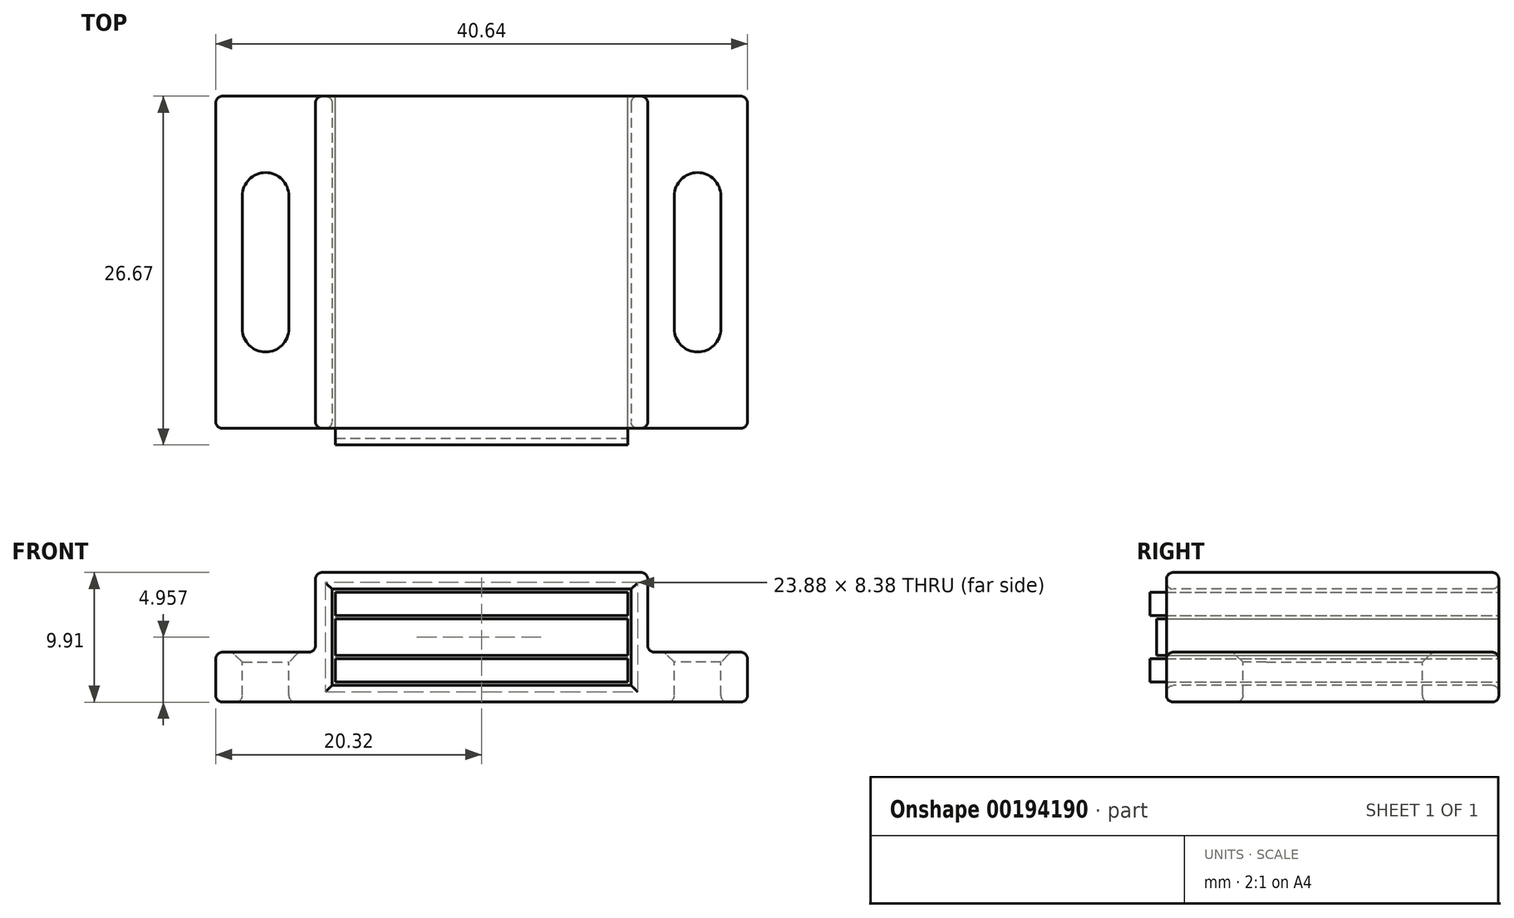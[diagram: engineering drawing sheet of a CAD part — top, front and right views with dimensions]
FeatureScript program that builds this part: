
annotation { "Feature Type Name" : "Feature", "Feature Type Description" : "" }
export const myFeature = defineFeature(function(context is Context, id is Id, definition is map)
    precondition{}
    {
        {
            var Q0;
            Q0=qCreatedBy(makeId("Front.planeOp"),FACE);
            var sketch = newSketch(context, id + "F0", { "sketchPlane" : qUnion([Q0])});
            skLineSegment(sketch, "E0", {"start": v(0, -9.9) * mm, "end": v(-40.64, -9.9) * mm});
            skLineSegment(sketch, "E1", {"start": v(-20.32, -9.9) * mm, "end": v(-20.32, 0) * mm, "construction": true});
            skLineSegment(sketch, "E2", {"start": v(-40.64, -9.9) * mm, "end": v(-40.64, -6.1) * mm});
            skLineSegment(sketch, "E3", {"start": v(-40.64, -6.1) * mm, "end": v(-33.02, -6.1) * mm});
            skLineSegment(sketch, "E4", {"start": v(-33.02, -6.1) * mm, "end": v(-33.02, 0) * mm});
            skLineSegment(sketch, "E5.MirrorCS", {"start": v(0, -9.9) * mm, "end": v(0, -6.1) * mm});
            skLineSegment(sketch, "E6.MirrorCS", {"start": v(0, -6.1) * mm, "end": v(-7.62, -6.1) * mm});
            skLineSegment(sketch, "E7.MirrorCS", {"start": v(-7.62, -6.1) * mm, "end": v(-7.62, 0) * mm});
            skLineSegment(sketch, "E8", {"start": v(-33.02, 0) * mm, "end": v(-7.62, 0) * mm});
            skLineSegment(sketch, "E9.0", {"start": v(-8.9, -8.64) * mm, "end": v(-8.9, -1.27) * mm});
            skLineSegment(sketch, "E9.1", {"start": v(-31.75, -1.27) * mm, "end": v(-8.89, -1.27) * mm});
            skLineSegment(sketch, "E9.2", {"start": v(-31.75, -8.64) * mm, "end": v(-31.75, -1.27) * mm});
            skLineSegment(sketch, "E10.0", {"start": v(-8.9, -8.64) * mm, "end": v(-31.75, -8.64) * mm});
            skSolve(sketch);
        }
        {
            var Q0;
            Q0=makeQuery(id+"F0.imprint","IMPRINT",FACE,{"disambiguationData":[TD([[makeQuery(id+"F0.imprint","IMPRINT",EDGE,{"derivedFrom":sQuery(id+"F0.wireOp",EDGE,"E0")}),-1.0]])]});
            extrude(context, id + "F1", {"entities" : qUnion([Q0]), "oppositeDirection" : true, "depth" : 25.4 * mm});
        }
        {
            var Q0;
            Q0=makeQuery(id+"F1.opExtrude","SWEPT_FACE",FACE,{"disambiguationData":[OSD([sQuery(id+"F0.wireOp",EDGE,"E8")])]});
            var sketch = newSketch(context, id + "F2", { "sketchPlane" : qUnion([Q0])});
            skLineSegment(sketch, "E11.0", {"start": v(-40.64, 25.4) * mm, "end": v(-40.64, 0) * mm, "construction": true});
            skLineSegment(sketch, "E11.1", {"start": v(-33.02, 25.4) * mm, "end": v(-33.02, 0) * mm, "construction": true});
            skLineSegment(sketch, "E11.2", {"start": v(-7.62, 25.4) * mm, "end": v(-7.62, 0) * mm, "construction": true});
            skLineSegment(sketch, "E11.3", {"start": v(0, 25.4) * mm, "end": v(0, 0) * mm, "construction": true});
            skLineSegment(sketch, "E12.0", {"start": v(-38.6, 17.78) * mm, "end": v(-38.6, 7.62) * mm});
            skLineSegment(sketch, "E13.0", {"start": v(-35.05, 17.78) * mm, "end": v(-35.05, 7.62) * mm});
            skLineSegment(sketch, "E14", {"start": v(-33.02, 25.4) * mm, "end": v(-7.62, 25.4) * mm, "construction": true});
            skLineSegment(sketch, "E15", {"start": v(-20.32, 25.4) * mm, "end": v(-20.32, 0) * mm, "construction": true});
            skArc(sketch, "E16", {"start": v(-35.05, 17.78) * mm, "mid": v(-36.83, 19.56) * mm, "end": v(-38.6, 17.78) * mm});
            skArc(sketch, "E17", {"start": v(-38.6, 7.62) * mm, "mid": v(-36.83, 5.84) * mm, "end": v(-35.05, 7.62) * mm});
            skLineSegment(sketch, "E18.MirrorCS", {"start": v(-2.03, 17.78) * mm, "end": v(-2.03, 7.62) * mm});
            skLineSegment(sketch, "E19.MirrorCS", {"start": v(-5.59, 17.78) * mm, "end": v(-5.59, 7.62) * mm});
            skArc(sketch, "E20.MirrorCS", {"start": v(-5.59, 17.78) * mm, "mid": v(-3.81, 19.56) * mm, "end": v(-2.03, 17.78) * mm});
            skArc(sketch, "E21.MirrorCS", {"start": v(-2.03, 7.62) * mm, "mid": v(-3.81, 5.84) * mm, "end": v(-5.59, 7.62) * mm});
            skSolve(sketch);
        }
        {
            var Q0;
            Q0=makeQuery(id+"F2.imprint","IMPRINT",FACE,{"disambiguationData":[TD([[makeQuery(id+"F2.imprint","IMPRINT",EDGE,{"derivedFrom":sQuery(id+"F2.wireOp",EDGE,"E12.0")}),1.0]])]});
            var Q1;
            Q1=makeQuery(id+"F2.imprint","IMPRINT",FACE,{"disambiguationData":[TD([[makeQuery(id+"F2.imprint","IMPRINT",EDGE,{"derivedFrom":sQuery(id+"F2.wireOp",EDGE,"E18.MirrorCS")}),-1.0]])]});
            extrude(context, id + "F3", {"entities" : qUnion([Q0, Q1]), "operationType" : NewBodyOperationType.REMOVE, "endBound" : BoundingType.THROUGH_ALL, "oppositeDirection" : true, "depth" : 25.4 * mm});
        }
        {
            var Q0;
            Q0=makeQuery(id+"F1.opExtrude","CAP_FACE",FACE,{"disambiguationData":[OSD([sQuery(id+"F0.wireOp",EDGE,"E0"),sQuery(id+"F0.wireOp",EDGE,"E2"),sQuery(id+"F0.wireOp",EDGE,"E3"),sQuery(id+"F0.wireOp",EDGE,"E4"),sQuery(id+"F0.wireOp",EDGE,"E5.MirrorCS"),sQuery(id+"F0.wireOp",EDGE,"E6.MirrorCS"),sQuery(id+"F0.wireOp",EDGE,"E7.MirrorCS"),sQuery(id+"F0.wireOp",EDGE,"E8"),sQuery(id+"F0.wireOp",EDGE,"E9.0"),sQuery(id+"F0.wireOp",EDGE,"E9.1"),sQuery(id+"F0.wireOp",EDGE,"E9.2"),sQuery(id+"F0.wireOp",EDGE,"E10.0")])],"isStart":true});
            var sketch = newSketch(context, id + "F4", { "sketchPlane" : qUnion([Q0])});
            skLineSegment(sketch, "E22.0", {"start": v(-31.75, -8.64) * mm, "end": v(-31.75, -1.27) * mm, "construction": true});
            skLineSegment(sketch, "E22.1", {"start": v(-31.75, -1.27) * mm, "end": v(-8.89, -1.27) * mm, "construction": true});
            skLineSegment(sketch, "E22.2", {"start": v(-8.9, -8.64) * mm, "end": v(-8.9, -1.27) * mm, "construction": true});
            skLineSegment(sketch, "E22.3", {"start": v(-8.9, -8.64) * mm, "end": v(-31.75, -8.64) * mm, "construction": true});
            skLineSegment(sketch, "E23.0", {"start": v(-9.14, -3.3) * mm, "end": v(-9.14, -1.52) * mm});
            skLineSegment(sketch, "E23.1", {"start": v(-31.5, -1.52) * mm, "end": v(-9.14, -1.52) * mm});
            skLineSegment(sketch, "E23.2", {"start": v(-31.5, -3.3) * mm, "end": v(-31.5, -1.52) * mm});
            skLineSegment(sketch, "E24", {"start": v(-31.5, -3.3) * mm, "end": v(-9.14, -3.3) * mm});
            skLineSegment(sketch, "E25", {"start": v(-31.75, -4.95) * mm, "end": v(-8.9, -4.95) * mm, "construction": true});
            skLineSegment(sketch, "E26.MirrorCS", {"start": v(-31.5, -8.38) * mm, "end": v(-9.14, -8.38) * mm});
            skLineSegment(sketch, "E27.MirrorCS", {"start": v(-31.5, -6.6) * mm, "end": v(-31.5, -8.38) * mm});
            skLineSegment(sketch, "E28.MirrorCS", {"start": v(-31.5, -6.6) * mm, "end": v(-9.14, -6.6) * mm});
            skLineSegment(sketch, "E29.MirrorCS", {"start": v(-9.14, -6.6) * mm, "end": v(-9.14, -8.38) * mm});
            skLineSegment(sketch, "E30.0", {"start": v(-31.5, -3.56) * mm, "end": v(-9.14, -3.56) * mm});
            skLineSegment(sketch, "E31.MirrorCS", {"start": v(-31.75, -2.16) * mm, "end": v(-8.9, -2.16) * mm, "construction": true});
            skLineSegment(sketch, "E32.MirrorCS", {"start": v(-31.5, -6.35) * mm, "end": v(-9.14, -6.35) * mm});
            skLineSegment(sketch, "E33", {"start": v(-31.5, -3.56) * mm, "end": v(-31.5, -6.35) * mm});
            skLineSegment(sketch, "E34", {"start": v(-9.14, -3.56) * mm, "end": v(-9.14, -6.35) * mm});
            skSolve(sketch);
        }
        {
            var Q0;
            Q0=makeQuery(id+"F4.imprint","IMPRINT",FACE,{"disambiguationData":[TD([[makeQuery(id+"F4.imprint","IMPRINT",EDGE,{"derivedFrom":sQuery(id+"F4.wireOp",EDGE,"E23.0")}),1.0]])]});
            extrude(context, id + "F5", {"entities" : qUnion([Q0]), "depth" : 1.27 * mm, "hasSecondDirection" : true, "secondDirectionOppositeDirection" : true, "secondDirectionDepth" : 25.4 * mm});
        }
        {
            var Q0;
            Q0=makeQuery(id+"F4.imprint","IMPRINT",FACE,{"disambiguationData":[TD([[makeQuery(id+"F4.imprint","IMPRINT",EDGE,{"derivedFrom":sQuery(id+"F4.wireOp",EDGE,"E26.MirrorCS")}),1.0]])]});
            extrude(context, id + "F6", {"entities" : qUnion([Q0]), "depth" : 1.27 * mm, "hasSecondDirection" : true, "secondDirectionOppositeDirection" : true, "secondDirectionDepth" : 25.4 * mm});
        }
        {
            var Q0;
            Q0=makeQuery(id+"F4.imprint","IMPRINT",FACE,{"disambiguationData":[TD([[makeQuery(id+"F4.imprint","IMPRINT",EDGE,{"derivedFrom":sQuery(id+"F4.wireOp",EDGE,"E30.0")}),-1.0]])]});
            extrude(context, id + "F7", {"entities" : qUnion([Q0]), "depth" : 0.76 * mm, "hasSecondDirection" : true, "secondDirectionOppositeDirection" : true, "secondDirectionDepth" : 25.4 * mm});
        }
        {
            var Q0;
            Q0=makeQuery(id+"F3.boolean.opBoolean","INTERSECT",EDGE,{"derivedFrom":[makeQuery(id+"F1.opExtrude","SWEPT_FACE",FACE,{"disambiguationData":[OSD([sQuery(id+"F0.wireOp",EDGE,"E3")])]}),makeQuery(id+"F3.opExtrude","SWEPT_FACE",FACE,{"disambiguationData":[OSD([sQuery(id+"F2.wireOp",EDGE,"E13.0")])]})]});
            var Q1;
            Q1=makeQuery(id+"F3.boolean.opBoolean","INTERSECT",EDGE,{"derivedFrom":[makeQuery(id+"F1.opExtrude","SWEPT_FACE",FACE,{"disambiguationData":[OSD([sQuery(id+"F0.wireOp",EDGE,"E6.MirrorCS")])]}),makeQuery(id+"F3.opExtrude","SWEPT_FACE",FACE,{"disambiguationData":[OSD([sQuery(id+"F2.wireOp",EDGE,"E18.MirrorCS")])]})]});
            chamfer(context, id + "F8", {"entities" : qUnion([Q0, Q1]), "width" : 0.76 * mm, "tangentPropagation" : true});
        }
        {
            var Q0;
            Q0=makeQuery(id+"F1.opExtrude","SWEPT_EDGE",EDGE,{"disambiguationData":[OSD([sQuery(id+"F0.wireOp",EDGE,"E3"),sQuery(id+"F0.wireOp",EDGE,"E4")])]});
            var Q1;
            Q1=makeQuery(id+"F1.opExtrude","SWEPT_EDGE",EDGE,{"disambiguationData":[OSD([sQuery(id+"F0.wireOp",EDGE,"E6.MirrorCS"),sQuery(id+"F0.wireOp",EDGE,"E7.MirrorCS")])]});
            var Q2;
            Q2=makeQuery(id+"F1.opExtrude","SWEPT_EDGE",EDGE,{"disambiguationData":[OSD([sQuery(id+"F0.wireOp",EDGE,"E7.MirrorCS"),sQuery(id+"F0.wireOp",EDGE,"E8")])]});
            var Q3;
            Q3=makeQuery(id+"F1.opExtrude","SWEPT_EDGE",EDGE,{"disambiguationData":[OSD([sQuery(id+"F0.wireOp",EDGE,"E4"),sQuery(id+"F0.wireOp",EDGE,"E8")])]});
            var Q4;
            Q4=makeQuery(id+"F1.opExtrude","SWEPT_FACE",FACE,{"disambiguationData":[OSD([sQuery(id+"F0.wireOp",EDGE,"E8")])]});
            var Q5;
            Q5=makeQuery(id+"F1.opExtrude","SWEPT_FACE",FACE,{"disambiguationData":[OSD([sQuery(id+"F0.wireOp",EDGE,"E4")])]});
            var Q6;
            Q6=makeQuery(id+"F1.opExtrude","SWEPT_FACE",FACE,{"disambiguationData":[OSD([sQuery(id+"F0.wireOp",EDGE,"E3")])]});
            var Q7;
            Q7=makeQuery(id+"F1.opExtrude","SWEPT_FACE",FACE,{"disambiguationData":[OSD([sQuery(id+"F0.wireOp",EDGE,"E2")])]});
            var Q8;
            Q8=makeQuery(id+"F1.opExtrude","SWEPT_FACE",FACE,{"disambiguationData":[OSD([sQuery(id+"F0.wireOp",EDGE,"E6.MirrorCS")])]});
            var Q9;
            Q9=makeQuery(id+"F1.opExtrude","SWEPT_FACE",FACE,{"disambiguationData":[OSD([sQuery(id+"F0.wireOp",EDGE,"E7.MirrorCS")])]});
            var Q10;
            Q10=makeQuery(id+"F1.opExtrude","CAP_FACE",FACE,{"disambiguationData":[OSD([sQuery(id+"F0.wireOp",EDGE,"E0"),sQuery(id+"F0.wireOp",EDGE,"E2"),sQuery(id+"F0.wireOp",EDGE,"E3"),sQuery(id+"F0.wireOp",EDGE,"E4"),sQuery(id+"F0.wireOp",EDGE,"E5.MirrorCS"),sQuery(id+"F0.wireOp",EDGE,"E6.MirrorCS"),sQuery(id+"F0.wireOp",EDGE,"E7.MirrorCS"),sQuery(id+"F0.wireOp",EDGE,"E8"),sQuery(id+"F0.wireOp",EDGE,"E9.0"),sQuery(id+"F0.wireOp",EDGE,"E9.1"),sQuery(id+"F0.wireOp",EDGE,"E9.2"),sQuery(id+"F0.wireOp",EDGE,"E10.0")])],"isStart":true});
            var Q11;
            Q11=makeQuery(id+"F1.opExtrude","SWEPT_FACE",FACE,{"disambiguationData":[OSD([sQuery(id+"F0.wireOp",EDGE,"E5.MirrorCS")])]});
            var Q12;
            Q12=makeQuery(id+"F1.opExtrude","SWEPT_FACE",FACE,{"disambiguationData":[OSD([sQuery(id+"F0.wireOp",EDGE,"E0")])]});
            var Q13;
            Q13=makeQuery(id+"F1.opExtrude","CAP_FACE",FACE,{"disambiguationData":[OSD([sQuery(id+"F0.wireOp",EDGE,"E0"),sQuery(id+"F0.wireOp",EDGE,"E2"),sQuery(id+"F0.wireOp",EDGE,"E3"),sQuery(id+"F0.wireOp",EDGE,"E4"),sQuery(id+"F0.wireOp",EDGE,"E5.MirrorCS"),sQuery(id+"F0.wireOp",EDGE,"E6.MirrorCS"),sQuery(id+"F0.wireOp",EDGE,"E7.MirrorCS"),sQuery(id+"F0.wireOp",EDGE,"E8"),sQuery(id+"F0.wireOp",EDGE,"E9.0"),sQuery(id+"F0.wireOp",EDGE,"E9.1"),sQuery(id+"F0.wireOp",EDGE,"E9.2"),sQuery(id+"F0.wireOp",EDGE,"E10.0")])],"isStart":false});
            fillet(context, id + "F9", {"entities" : qUnion([Q0, Q1, Q2, Q3, Q4, Q5, Q6, Q7, Q8, Q9, Q10, Q11, Q12, Q13]), "radius" : 0.5 * mm, "tangentPropagation" : true, "allowEdgeOverflow" : false});
        }
    });
